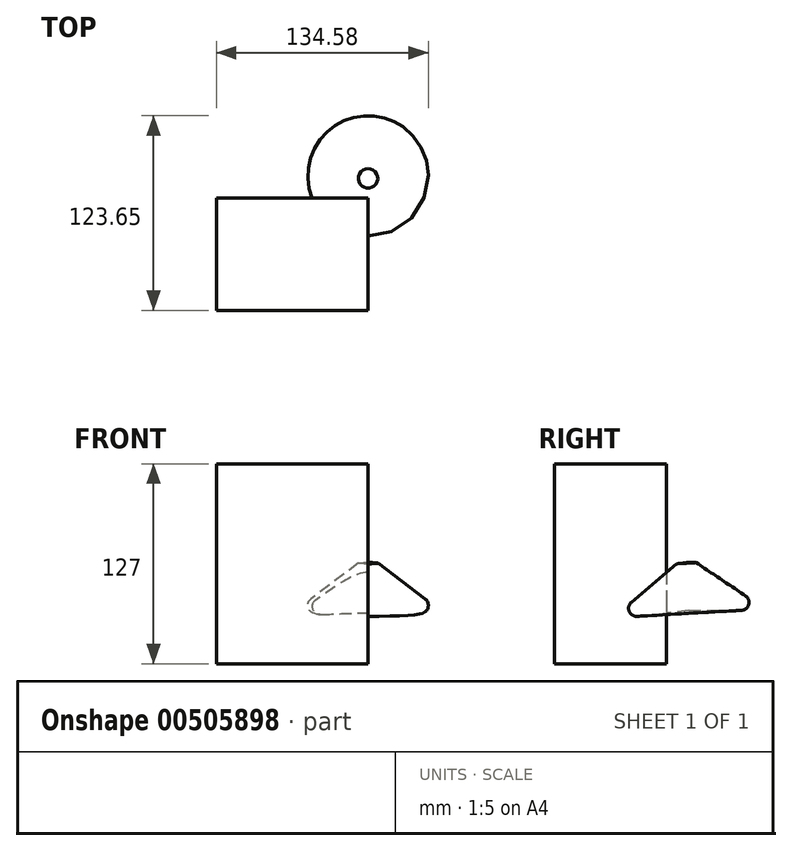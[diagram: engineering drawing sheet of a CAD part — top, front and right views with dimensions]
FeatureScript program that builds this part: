
annotation { "Feature Type Name" : "Feature", "Feature Type Description" : "" }
export const myFeature = defineFeature(function(context is Context, id is Id, definition is map)
    precondition{}
    {
        {
            var Q0;
            Q0=qCreatedBy(makeId("Top.planeOp"),FACE);
            var sketch = newSketch(context, id + "F0", { "sketchPlane" : qUnion([Q0])});
            skLineSegment(sketch, "E0.bottom", {"start": v(-49.34, -11.7) * mm, "end": v(46.94, -11.7) * mm});
            skLineSegment(sketch, "E0.top", {"start": v(-49.34, 59.54) * mm, "end": v(46.94, 59.54) * mm});
            skLineSegment(sketch, "E0.left", {"start": v(-49.34, -11.7) * mm, "end": v(-49.34, 59.54) * mm});
            skLineSegment(sketch, "E0.right", {"start": v(46.94, -11.7) * mm, "end": v(46.94, 59.54) * mm});
            skSolve(sketch);
        }
        {
            var Q0;
            Q0=makeQuery(id+"F0.imprint","IMPRINT",FACE,{"disambiguationData":[TD([[makeQuery(id+"F0.imprint","IMPRINT",EDGE,{"derivedFrom":sQuery(id+"F0.wireOp",EDGE,"E0.bottom")}),1.0]])]});
            extrude(context, id + "F1", {"entities" : qUnion([Q0]), "depth" : 127 * mm});
        }
        {
            var Q0;
            Q0=makeQuery(id+"F1.opExtrude","SWEPT_FACE",FACE,{"disambiguationData":[OSD([sQuery(id+"F0.wireOp",EDGE,"E0.right")])]});
            var sketch = newSketch(context, id + "F2", { "sketchPlane" : qUnion([Q0])});
            skLineSegment(sketch, "E1", {"start": v(72.16, 64.27) * mm, "end": v(78.36, 64.27) * mm});
            skLineSegment(sketch, "E2", {"start": v(78.36, 64.27) * mm, "end": v(123.56, 33.94) * mm});
            skLineSegment(sketch, "E3", {"start": v(123.56, 33.94) * mm, "end": v(73.9, 33.94) * mm});
            skLineSegment(sketch, "E4", {"start": v(73.9, 33.94) * mm, "end": v(72.16, 64.27) * mm});
            skLineSegment(sketch, "E5", {"start": v(101.73, -20.74) * mm, "end": v(-160.22, 258.24) * mm});
            skSolve(sketch);
        }
        {
            var Q0;
            Q0=makeQuery(id+"F2.imprint","IMPRINT",FACE,{"disambiguationData":[TD([[makeQuery(id+"F2.imprint","IMPRINT",EDGE,{"derivedFrom":sQuery(id+"F2.wireOp",EDGE,"E1")}),-1.0]])]});
            var Q1;
            Q1=sQuery(id+"F2.wireOp",EDGE,"E1");
            var Q2;
            Q2=sQuery(id+"F2.wireOp",EDGE,"E2");
            var Q3;
            Q3=sQuery(id+"F2.wireOp",EDGE,"E4");
            var Q4;
            Q4=sQuery(id+"F2.wireOp",EDGE,"E3");
            var Q5;
            Q5=sQuery(id+"F2.wireOp",EDGE,"E4");
            revolve(context, id + "F3", {"operationType" : NewBodyOperationType.ADD, "entities" : qUnion([Q0]), "surfaceEntities" : qUnion([Q1, Q2, Q3, Q4]), "axis" : qUnion([Q5]), "revolveType" : RevolveType.FULL});
        }
        {
            var Q0;
            Q0=makeQuery(id+"F3.opRevolve","SWEPT_EDGE",EDGE,{"disambiguationData":[OSD([sQuery(id+"F2.wireOp",EDGE,"E2"),sQuery(id+"F2.wireOp",EDGE,"E3")])]});
            fillet(context, id + "F4", {"entities" : qUnion([Q0]), "radius" : 5.08 * mm, "tangentPropagation" : true, "allowEdgeOverflow" : false});
        }
    });
